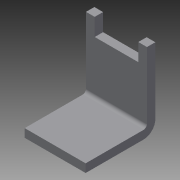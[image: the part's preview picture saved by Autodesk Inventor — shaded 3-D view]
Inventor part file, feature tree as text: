
AUTODESK INVENTOR PART (.ipt)
format: ipt  version: 2013 (Build 170138000, 138)  size: 101,376 bytes
history: native  units: in
note: dims shown in document units (in); Inventor stores cm internally (conversion verified against a paired STEP export)
features: sheet_metal_op x4, sketch x2, other x2
ambient origin geometry x8: Origin, YZ Plane, XZ Plane, XY Plane, X Axis, Y Axis, Z Axis, Center Point
bodies: Solid1 (feature_tree)
feature tree (8):
  sheet_metal_op  "Face1"
  sheet_metal_op  "Flange1"
  sketch  "Sketch1"  dims[d0=0.25in]
  other  "Plate1"
  sketch  "Sketch2"  dims[d1=0.125in d2=0.375in d3=0.625in d4=0.125in d6=0.75in d12=0.12in d13=0.12in d14=0.06in d15=0.24in d16=0.12in d17=1.0in d18=90.0deg d19=0.05in d20=0.48in d21=0.12in d22=0.12in]
  other  "Plate2"
  sheet_metal_op  "Bend1"
  sheet_metal_op  "Corner1"
